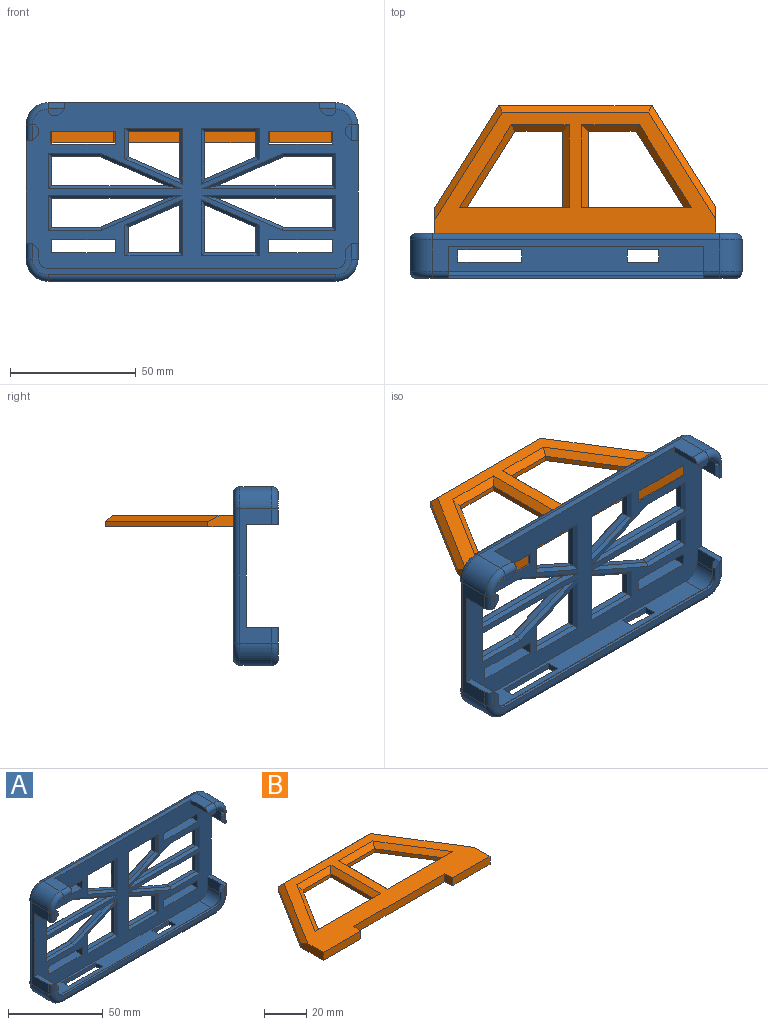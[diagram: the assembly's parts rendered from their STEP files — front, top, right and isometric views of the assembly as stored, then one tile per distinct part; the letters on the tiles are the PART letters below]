
ASSEMBLY  parts=2 mates=1
PART A: 200 faces, bbox 133.5x17.8x72.6 mm
  f0: plane 114.3x10.16mm, normal (0,0,1), area 967.7mm2, adj f8,f9,f12,f91,f192,f193,f194,f195
  f1: plane 114.3x12.7mm, normal (0,0,-1), area 1258.1mm2, adj f17,f18,f96,f106,f192,f193,f194,f195
  f2: plane 6.35x2.54mm, normal (0,-1,0), area 12.1mm2, adj f92,f93,f114,f185,f188
  f3: plane 6.35x2.54mm, normal (0,-1,0), area 12.1mm2, adj f80,f81,f111,f187,f191
  f4: plane 10.16x6.35mm, normal (1,0,0), area 64.5mm2, adj f12,f74,f75,f190
  f5: plane 10.16x6.35mm, normal (-1,0,0), area 64.5mm2, adj f12,f70,f71,f188
  f6: plane 10.16x6.35mm, normal (-1,0,0), area 64.5mm2, adj f8,f12,f77,f91
  f7: plane 10.16x6.35mm, normal (1,0,0), area 64.5mm2, adj f9,f12,f78,f91
  f8: cylinder r=6.35mm len=10.16mm, axis (0,1,0), area 101.3mm2, adj f0,f6,f12,f91
  f9: cylinder r=6.35mm len=10.16mm, axis (0,1,0), area 101.3mm2, adj f0,f7,f12,f91
  f10: plane 10.16x6.35mm, normal (0,0,-1), area 64.5mm2, adj f12,f69,f70,f189
  f11: plane 10.16x6.35mm, normal (0,0,-1), area 64.5mm2, adj f12,f73,f75,f191
  f12: plane 132.08x68.58mm, normal (0,-1,0), area 4649.6mm2, adj f0,f4,f5,f6,f7,f8,f9,f10
  f13: cylinder r=8.89mm len=12.7mm, axis (0,1,0), area 177.3mm2, adj f14,f67,f101,f113
  f14: plane 114.3x12.7mm, normal (0,0,1), area 419.4mm2, adj f12,f13,f15,f69,f73,f103,f111,f112
  f15: cylinder r=8.89mm len=12.7mm, axis (0,1,0), area 177.3mm2, adj f14,f16,f102,f110
  f16: plane 53.34x12.7mm, normal (-1,0,0), area 264.5mm2, adj f12,f15,f17,f74,f78,f100,f108,f109
  f17: cylinder r=8.89mm len=12.7mm, axis (0,1,0), area 177.3mm2, adj f1,f16,f98,f107
  f18: cylinder r=8.89mm len=12.7mm, axis (0,1,0), area 177.3mm2, adj f1,f67,f97,f105
  f19: plane 25.4x5.08mm, normal (0,0,-1), area 129mm2, adj f12,f20,f55,f68
  f20: plane 5.08x5.08mm, normal (-1,0,0), area 25.8mm2, adj f12,f19,f21,f68
  f21: plane 25.4x5.08mm, normal (0,0,1), area 129mm2, adj f12,f20,f55,f68
  f22: plane 25.4x5.08mm, normal (0,0,1), area 129mm2, adj f12,f23,f56,f68
  f23: plane 5.08x5.08mm, normal (1,0,0), area 25.8mm2, adj f12,f22,f24,f68
  f24: plane 25.4x5.08mm, normal (0,0,-1), area 129mm2, adj f12,f23,f56,f68
  f25: plane 5.08x5.08mm, normal (1,0,0), area 25.8mm2, adj f12,f26,f57,f68
  f26: plane 25.4x5.08mm, normal (0,0,-1), area 129mm2, adj f12,f25,f27,f68
  f27: plane 5.08x5.08mm, normal (-1,0,0), area 25.8mm2, adj f12,f26,f57,f68
  f28: plane 5.08x5.08mm, normal (1,0,0), area 25.8mm2, adj f12,f29,f58,f68
  f29: plane 25.4x5.08mm, normal (0,0,-1), area 129mm2, adj f12,f28,f30,f68
  f30: plane 5.08x5.08mm, normal (-1,0,0), area 25.8mm2, adj f12,f29,f58,f68
  f31: plane 26.13x11.43mm, normal (0.4,0,0.92), area 72.4mm2, adj f32,f59,f134,f151
  f32: plane 45.72x2.54mm, normal (0,0,-1), area 116.1mm2, adj f31,f33,f132,f152
  f33: plane 11.43x2.54mm, normal (-1,0,0), area 29mm2, adj f32,f59,f131,f154
  f34: plane 19.05x2.54mm, normal (1,0,0), area 48.4mm2, adj f35,f60,f130,f147
  f35: plane 20.32x8.89mm, normal (-0.4,0,-0.92), area 56.3mm2, adj f34,f36,f129,f148
  f36: plane 10.16x2.54mm, normal (-1,0,0), area 25.8mm2, adj f35,f60,f127,f150
  f37: plane 20.32x2.54mm, normal (0,0,-1), area 51.6mm2, adj f38,f61,f145,f165
  f38: plane 19.05x2.54mm, normal (-1,0,0), area 48.4mm2, adj f37,f39,f143,f163
  f39: plane 20.32x8.89mm, normal (0.4,0,0.92), area 56.3mm2, adj f38,f61,f144,f164
  f40: plane 20.32x8.89mm, normal (0.4,0,-0.92), area 56.3mm2, adj f41,f62,f126,f176
  f41: plane 19.05x2.54mm, normal (-1,0,0), area 48.4mm2, adj f40,f42,f124,f175
  f42: plane 20.32x2.54mm, normal (0,0,1), area 51.6mm2, adj f41,f62,f123,f177
  f43: plane 45.72x2.54mm, normal (0,0,-1), area 116.1mm2, adj f44,f63,f122,f174
  f44: plane 26.13x11.43mm, normal (-0.4,0,0.92), area 72.4mm2, adj f43,f45,f120,f172
  f45: plane 19.59x2.54mm, normal (0,0,1), area 49.8mm2, adj f44,f63,f119,f171
  f46: plane 26.13x11.43mm, normal (-0.4,0,-0.92), area 72.4mm2, adj f47,f64,f118,f170
  f47: plane 45.72x2.54mm, normal (0,0,1), area 116.1mm2, adj f46,f48,f116,f168
  f48: plane 11.43x2.54mm, normal (1,0,0), area 29mm2, adj f47,f64,f115,f167
  f49: plane 19.59x2.54mm, normal (0,0,-1), area 49.8mm2, adj f50,f65,f135,f157
  f50: plane 11.43x2.54mm, normal (-1,0,0), area 29mm2, adj f49,f51,f137,f158
  f51: plane 45.72x2.54mm, normal (0,0,1), area 116.1mm2, adj f50,f65,f138,f156
  f52: plane 19.05x2.54mm, normal (1,0,0), area 48.4mm2, adj f53,f66,f140,f160
  f53: plane 20.32x2.54mm, normal (0,0,-1), area 51.6mm2, adj f52,f54,f139,f162
  f54: plane 10.16x2.54mm, normal (-1,0,0), area 25.8mm2, adj f53,f66,f141,f161
  f55: plane 5.08x5.08mm, normal (1,0,0), area 25.8mm2, adj f12,f19,f21,f68
  f56: plane 5.08x5.08mm, normal (-1,0,0), area 25.8mm2, adj f12,f22,f24,f68
  f57: plane 25.4x5.08mm, normal (0,0,1), area 129mm2, adj f12,f25,f27,f68
  f58: plane 25.4x5.08mm, normal (0,0,1), area 129mm2, adj f12,f28,f30,f68
  f59: plane 19.59x2.54mm, normal (0,0,1), area 49.8mm2, adj f31,f33,f133,f153
  f60: plane 20.32x2.54mm, normal (0,0,1), area 51.6mm2, adj f34,f36,f128,f149
  f61: plane 10.16x2.54mm, normal (1,0,0), area 25.8mm2, adj f37,f39,f146,f166
  f62: plane 10.16x2.54mm, normal (1,0,0), area 25.8mm2, adj f40,f42,f125,f178
  f63: plane 11.43x2.54mm, normal (1,0,0), area 29mm2, adj f43,f45,f121,f173
  f64: plane 19.59x2.54mm, normal (0,0,-1), area 49.8mm2, adj f46,f48,f117,f169
  f65: plane 26.13x11.43mm, normal (0.4,0,-0.92), area 72.4mm2, adj f49,f51,f136,f155
  f66: plane 20.32x8.89mm, normal (-0.4,0,0.92), area 56.3mm2, adj f52,f54,f142,f159
  f67: plane 53.34x12.7mm, normal (1,0,0), area 264.5mm2, adj f12,f13,f18,f71,f77,f99,f104,f114
  f68: plane 127x66.04mm, normal (0,1,0), area 4185.1mm2, adj f19,f20,f21,f22,f23,f24,f25,f26
  f69: plane 12.7x2.54mm, normal (-1,0,0), area 30.9mm2, adj f10,f12,f14,f83,f112
  f70: cylinder r=6.35mm len=12.7mm, axis (0,1,0), area 126.7mm2, adj f5,f10,f12,f82,f93,f113
  f71: plane 12.7x2.54mm, normal (0,0,-1), area 30.9mm2, adj f5,f12,f67,f92,f114
  f72: plane 6.35x2.54mm, normal (0,-1,0), area 12.1mm2, adj f82,f83,f112,f184,f189
  f73: plane 12.7x2.54mm, normal (1,0,0), area 30.9mm2, adj f11,f12,f14,f80,f111
  f74: plane 12.7x2.54mm, normal (0,0,-1), area 30.9mm2, adj f4,f12,f16,f95,f109
  f75: cylinder r=6.35mm len=12.7mm, axis (0,1,0), area 126.7mm2, adj f4,f11,f12,f81,f94,f110
  f76: plane 6.35x2.54mm, normal (0,-1,0), area 12.1mm2, adj f94,f95,f109,f186,f190
  f77: plane 12.7x2.54mm, normal (0,0,1), area 30.9mm2, adj f6,f12,f67,f84,f104
  f78: plane 12.7x2.54mm, normal (0,0,1), area 30.9mm2, adj f7,f12,f16,f90,f108
  f79: plane 127x12.7mm, normal (0,-1,0), area 356.7mm2, adj f84,f85,f86,f87,f88,f89,f90,f104
  f80: plane 2.54x2.54mm, normal (0.71,0,-0.71), area 4.6mm2, adj f3,f73,f191
  f81: plane 2.54x1.27mm, normal (-1,0,0), area 2.4mm2, adj f3,f75,f187,f191
  f82: plane 2.54x1.27mm, normal (1,0,0), area 2.4mm2, adj f70,f72,f184,f189
  f83: plane 2.54x2.54mm, normal (-0.71,0,-0.71), area 4.6mm2, adj f69,f72,f189
  f84: plane 2.54x2.54mm, normal (-0.71,0,0.71), area 8mm2, adj f77,f79,f85,f91,f183
  f85: plane 3.81x1.27mm, normal (-1,0,0), area 4.8mm2, adj f79,f84,f86,f183
  f86: cylinder r=3.81mm len=3.81mm, axis (0,1,0), area 7.6mm2, adj f79,f85,f87,f182
  f87: plane 114.3x1.27mm, normal (0,0,1), area 145.2mm2, adj f79,f86,f88,f181
  f88: cylinder r=3.81mm len=3.81mm, axis (0,1,0), area 7.6mm2, adj f79,f87,f89,f180
  f89: plane 3.81x1.27mm, normal (1,0,0), area 4.8mm2, adj f79,f88,f90,f179
  f90: plane 2.54x2.54mm, normal (0.71,0,0.71), area 8mm2, adj f78,f79,f89,f91,f179
  f91: plane 127x12.7mm, normal (0,1,0), area 182.5mm2, adj f0,f6,f7,f8,f9,f84,f90,f179
  f92: plane 2.54x2.54mm, normal (-0.71,0,-0.71), area 4.6mm2, adj f2,f71,f188
  f93: plane 2.54x1.27mm, normal (0,0,1), area 2.4mm2, adj f2,f70,f185,f188
  f94: plane 2.54x1.27mm, normal (0,0,1), area 2.4mm2, adj f75,f76,f186,f190
  f95: plane 2.54x2.54mm, normal (0.71,0,-0.71), area 4.6mm2, adj f74,f76,f190
  f96: cylinder r=2.54mm len=114.3mm, axis (1,0,0), area 456mm2, adj f1,f68,f97,f98
  f97: torus R=6.35mm, axis (0,-1,0), area 49.9mm2, adj f18,f68,f96,f99
  f98: torus R=6.35mm, axis (0,-1,0), area 49.9mm2, adj f17,f68,f96,f100
  f99: cylinder r=2.54mm len=53.34mm, axis (0,0,1), area 212.8mm2, adj f67,f68,f97,f101
  f100: cylinder r=2.54mm len=53.34mm, axis (0,0,-1), area 212.8mm2, adj f16,f68,f98,f102
  f101: torus R=6.35mm, axis (0,-1,0), area 49.9mm2, adj f13,f68,f99,f103
  f102: torus R=6.35mm, axis (0,-1,0), area 49.9mm2, adj f15,f68,f100,f103
  f103: cylinder r=2.54mm len=114.3mm, axis (-1,0,0), area 456mm2, adj f14,f68,f101,f102
  f104: cylinder r=2.54mm len=6.35mm, axis (0,0,-1), area 25.3mm2, adj f67,f77,f79,f105
  f105: torus R=6.35mm, axis (0,-1,0), area 49.9mm2, adj f18,f79,f104,f106
  f106: cylinder r=2.54mm len=114.3mm, axis (-1,0,0), area 456mm2, adj f1,f79,f105,f107
  f107: torus R=6.35mm, axis (0,-1,0), area 49.9mm2, adj f17,f79,f106,f108
  f108: cylinder r=2.54mm len=6.35mm, axis (0,0,1), area 25.3mm2, adj f16,f78,f79,f107
  f109: cylinder r=2.54mm len=6.35mm, axis (0,0,1), area 25.3mm2, adj f16,f74,f76,f110
  f110: torus R=6.35mm, axis (0,-1,0), area 49.9mm2, adj f15,f75,f109,f111
  f111: cylinder r=2.54mm len=6.35mm, axis (1,0,0), area 25.3mm2, adj f3,f14,f73,f110
  f112: cylinder r=2.54mm len=6.35mm, axis (1,0,0), area 25.3mm2, adj f14,f69,f72,f113
  f113: torus R=6.35mm, axis (0,-1,0), area 49.9mm2, adj f13,f70,f112,f114
  f114: cylinder r=2.54mm len=6.35mm, axis (0,0,-1), area 25.3mm2, adj f2,f67,f71,f113
  f115: plane 13.97x1.27mm, normal (0.71,-0.71,0), area 22.8mm2, adj f12,f48,f116,f117
  f116: plane 53.06x1.27mm, normal (0,-0.71,0.71), area 88.7mm2, adj f12,f47,f115,f118
  f117: plane 21.13x1.27mm, normal (0,-0.71,-0.71), area 36.6mm2, adj f12,f64,f115,f118
  f118: plane 32.2x13.97mm, normal (-0.28,-0.71,-0.65), area 56.9mm2, adj f12,f46,f116,f117
  f119: plane 21.13x1.27mm, normal (0,-0.71,0.71), area 36.6mm2, adj f12,f45,f120,f121
  f120: plane 32.2x13.97mm, normal (-0.28,-0.71,0.65), area 56.9mm2, adj f12,f44,f119,f122
  f121: plane 13.97x1.27mm, normal (0.71,-0.71,0), area 22.8mm2, adj f12,f63,f119,f122
  f122: plane 53.06x1.27mm, normal (0,-0.71,-0.71), area 88.7mm2, adj f12,f43,f120,f121
  f123: plane 22.86x1.27mm, normal (0,-0.71,0.71), area 38.8mm2, adj f12,f42,f124,f125
  f124: plane 22.26x1.27mm, normal (-0.71,-0.71,0), area 37.1mm2, adj f12,f41,f123,f126
  f125: plane 12.26x1.27mm, normal (0.71,-0.71,0), area 20.1mm2, adj f12,f62,f123,f126
  f126: plane 22.86x10.83mm, normal (0.28,-0.71,-0.65), area 42.3mm2, adj f12,f40,f124,f125
  f127: plane 12.26x1.27mm, normal (-0.71,-0.71,0), area 20.1mm2, adj f12,f36,f128,f129
  f128: plane 22.86x1.27mm, normal (0,-0.71,0.71), area 38.8mm2, adj f12,f60,f127,f130
  f129: plane 22.86x10.83mm, normal (-0.28,-0.71,-0.65), area 42.3mm2, adj f12,f35,f127,f130
  f130: plane 22.26x1.27mm, normal (0.71,-0.71,0), area 37.1mm2, adj f12,f34,f128,f129
  f131: plane 13.97x1.27mm, normal (-0.71,-0.71,0), area 22.8mm2, adj f12,f33,f132,f133
  f132: plane 53.06x1.27mm, normal (0,-0.71,-0.71), area 88.7mm2, adj f12,f32,f131,f134
  f133: plane 21.13x1.27mm, normal (0,-0.71,0.71), area 36.6mm2, adj f12,f59,f131,f134
  f134: plane 32.2x13.97mm, normal (0.28,-0.71,0.65), area 56.9mm2, adj f12,f31,f132,f133
  f135: plane 21.13x1.27mm, normal (0,-0.71,-0.71), area 36.6mm2, adj f12,f49,f136,f137
  f136: plane 32.2x13.97mm, normal (0.28,-0.71,-0.65), area 56.9mm2, adj f12,f65,f135,f138
  f137: plane 13.97x1.27mm, normal (-0.71,-0.71,0), area 22.8mm2, adj f12,f50,f135,f138
  f138: plane 53.06x1.27mm, normal (0,-0.71,0.71), area 88.7mm2, adj f12,f51,f136,f137
  f139: plane 22.86x1.27mm, normal (0,-0.71,-0.71), area 38.8mm2, adj f12,f53,f140,f141
  f140: plane 22.26x1.27mm, normal (0.71,-0.71,0), area 37.1mm2, adj f12,f52,f139,f142
  f141: plane 12.26x1.27mm, normal (-0.71,-0.71,0), area 20.1mm2, adj f12,f54,f139,f142
  f142: plane 22.86x10.83mm, normal (-0.28,-0.71,0.65), area 42.3mm2, adj f12,f66,f140,f141
  f143: plane 22.26x1.27mm, normal (-0.71,-0.71,0), area 37.1mm2, adj f12,f38,f144,f145
  f144: plane 22.86x10.83mm, normal (0.28,-0.71,0.65), area 42.3mm2, adj f12,f39,f143,f146
  f145: plane 22.86x1.27mm, normal (0,-0.71,-0.71), area 38.8mm2, adj f12,f37,f143,f146
  f146: plane 12.26x1.27mm, normal (0.71,-0.71,0), area 20.1mm2, adj f12,f61,f144,f145
  f147: plane 22.26x1.27mm, normal (0.71,0.71,0), area 37.1mm2, adj f34,f68,f148,f149
  f148: plane 22.86x10.83mm, normal (-0.28,0.71,-0.65), area 42.3mm2, adj f35,f68,f147,f150
  f149: plane 22.86x1.27mm, normal (0,0.71,0.71), area 38.8mm2, adj f60,f68,f147,f150
  f150: plane 12.26x1.27mm, normal (-0.71,0.71,0), area 20.1mm2, adj f36,f68,f148,f149
  f151: plane 32.2x13.97mm, normal (0.28,0.71,0.65), area 56.9mm2, adj f31,f68,f152,f153
  f152: plane 53.06x1.27mm, normal (0,0.71,-0.71), area 88.7mm2, adj f32,f68,f151,f154
  f153: plane 21.13x1.27mm, normal (0,0.71,0.71), area 36.6mm2, adj f59,f68,f151,f154
  f154: plane 13.97x1.27mm, normal (-0.71,0.71,0), area 22.8mm2, adj f33,f68,f152,f153
  f155: plane 32.2x13.97mm, normal (0.28,0.71,-0.65), area 56.9mm2, adj f65,f68,f156,f157
  f156: plane 53.06x1.27mm, normal (0,0.71,0.71), area 88.7mm2, adj f51,f68,f155,f158
  f157: plane 21.13x1.27mm, normal (0,0.71,-0.71), area 36.6mm2, adj f49,f68,f155,f158
  f158: plane 13.97x1.27mm, normal (-0.71,0.71,0), area 22.8mm2, adj f50,f68,f156,f157
  f159: plane 22.86x10.83mm, normal (-0.28,0.71,0.65), area 42.3mm2, adj f66,f68,f160,f161
  f160: plane 22.26x1.27mm, normal (0.71,0.71,0), area 37.1mm2, adj f52,f68,f159,f162
  f161: plane 12.26x1.27mm, normal (-0.71,0.71,0), area 20.1mm2, adj f54,f68,f159,f162
  f162: plane 22.86x1.27mm, normal (0,0.71,-0.71), area 38.8mm2, adj f53,f68,f160,f161
  f163: plane 22.26x1.27mm, normal (-0.71,0.71,0), area 37.1mm2, adj f38,f68,f164,f165
  f164: plane 22.86x10.83mm, normal (0.28,0.71,0.65), area 42.3mm2, adj f39,f68,f163,f166
  f165: plane 22.86x1.27mm, normal (0,0.71,-0.71), area 38.8mm2, adj f37,f68,f163,f166
  f166: plane 12.26x1.27mm, normal (0.71,0.71,0), area 20.1mm2, adj f61,f68,f164,f165
  f167: plane 13.97x1.27mm, normal (0.71,0.71,0), area 22.8mm2, adj f48,f68,f168,f169
  f168: plane 53.06x1.27mm, normal (0,0.71,0.71), area 88.7mm2, adj f47,f68,f167,f170
  f169: plane 21.13x1.27mm, normal (0,0.71,-0.71), area 36.6mm2, adj f64,f68,f167,f170
  f170: plane 32.2x13.97mm, normal (-0.28,0.71,-0.65), area 56.9mm2, adj f46,f68,f168,f169
  f171: plane 21.13x1.27mm, normal (0,0.71,0.71), area 36.6mm2, adj f45,f68,f172,f173
  f172: plane 32.2x13.97mm, normal (-0.28,0.71,0.65), area 56.9mm2, adj f44,f68,f171,f174
  f173: plane 13.97x1.27mm, normal (0.71,0.71,0), area 22.8mm2, adj f63,f68,f171,f174
  f174: plane 53.06x1.27mm, normal (0,0.71,-0.71), area 88.7mm2, adj f43,f68,f172,f173
  f175: plane 22.26x1.27mm, normal (-0.71,0.71,0), area 37.1mm2, adj f41,f68,f176,f177
  f176: plane 22.86x10.83mm, normal (0.28,0.71,-0.65), area 42.3mm2, adj f40,f68,f175,f178
  f177: plane 22.86x1.27mm, normal (0,0.71,0.71), area 38.8mm2, adj f42,f68,f175,f178
  f178: plane 12.26x1.27mm, normal (0.71,0.71,0), area 20.1mm2, adj f62,f68,f176,f177
  f179: plane 5.08x1.27mm, normal (0.71,0.71,0), area 8mm2, adj f89,f90,f91,f180
  f180: cone r=5.08mm half-angle=45deg, axis (0,1,0), area 12.5mm2, adj f88,f91,f179,f181
  f181: plane 114.3x1.27mm, normal (0,0.71,0.71), area 205.3mm2, adj f87,f91,f180,f182
  f182: cone r=5.08mm half-angle=45deg, axis (0,1,0), area 12.5mm2, adj f86,f91,f181,f183
  f183: plane 5.08x1.27mm, normal (-0.71,0.71,0), area 8mm2, adj f84,f85,f91,f182
  f184: plane 1.27x1.27mm, normal (0.71,0,-0.71), area 1.1mm2, adj f72,f82,f189
  f185: plane 1.27x1.27mm, normal (-0.71,0,0.71), area 1.1mm2, adj f2,f93,f188
  f186: plane 1.27x1.27mm, normal (0.71,0,0.71), area 1.1mm2, adj f76,f94,f190
  f187: plane 1.27x1.27mm, normal (-0.71,0,-0.71), area 1.1mm2, adj f3,f81,f191
  f188: plane 6.35x2.54mm, normal (-0.71,0.71,0), area 17.1mm2, adj f2,f5,f92,f93,f185
  f189: plane 6.35x2.54mm, normal (0,0.71,-0.71), area 17.1mm2, adj f10,f72,f82,f83,f184
  f190: plane 6.35x2.54mm, normal (0.71,0.71,0), area 17.1mm2, adj f4,f76,f94,f95,f186
  f191: plane 6.35x2.54mm, normal (0,0.71,-0.71), area 17.1mm2, adj f3,f11,f80,f81,f187
  f192: plane 5.08x2.54mm, normal (-1,0,0), area 12.9mm2, adj f0,f1,f193,f195
  f193: plane 12.7x2.54mm, normal (0,1,0), area 32.3mm2, adj f0,f1,f192,f194
  f194: plane 5.08x2.54mm, normal (1,0,0), area 12.9mm2, adj f0,f1,f193,f195
  f195: plane 12.7x2.54mm, normal (0,-1,0), area 32.3mm2, adj f0,f1,f192,f194
  f196: plane 5.08x2.54mm, normal (-1,0,0), area 12.9mm2, adj f0,f1,f197,f199
  f197: plane 25.4x2.54mm, normal (0,1,0), area 64.5mm2, adj f0,f1,f196,f198
  f198: plane 5.08x2.54mm, normal (1,0,0), area 12.9mm2, adj f0,f1,f197,f199
  f199: plane 25.4x2.54mm, normal (0,-1,0), area 64.5mm2, adj f0,f1,f196,f198
PART B: 29 faces, bbox 111.8x55.9x4.6 mm
  f0: plane 30.48x19.05mm, normal (-0.85,-0.53,0), area 73mm2, adj f1,f17,f19,f23
  f1: plane 43.64x4.57mm, normal (0,1,0), area 181.2mm2, adj f0,f2,f18,f19,f23,f25
  f2: plane 30.48x2.03mm, normal (1,0,0), area 61.9mm2, adj f1,f17,f19,f25
  f3: plane 5.08x4.57mm, normal (-1,-0.09,0), area 23.3mm2, adj f4,f15,f18,f19
  f4: plane 24.96x4.57mm, normal (0,-1,0), area 114.1mm2, adj f3,f5,f18,f19
  f5: plane 15.24x4.57mm, normal (1,0,0), area 63.6mm2, adj f4,f6,f18,f19,f28
  f6: plane 40.64x25.4mm, normal (0.85,0.53,0), area 97.4mm2, adj f5,f7,f19,f28
  f7: plane 60.96x2.03mm, normal (0,1,0), area 123.9mm2, adj f6,f8,f19,f27
  f8: plane 40.64x25.4mm, normal (-0.85,0.53,0), area 97.4mm2, adj f7,f9,f19,f26
  f9: plane 15.24x4.57mm, normal (-1,0,0), area 63.6mm2, adj f8,f10,f18,f19,f26
  f10: plane 24.96x4.57mm, normal (0,-1,0), area 114.1mm2, adj f9,f11,f18,f19
  f11: plane 5.08x4.57mm, normal (1,-0.09,0), area 23.3mm2, adj f10,f15,f18,f19
  f12: plane 30.48x19.05mm, normal (0.85,-0.53,0), area 73mm2, adj f13,f16,f19,f22
  f13: plane 19.05x2.03mm, normal (0,-1,0), area 38.7mm2, adj f12,f14,f19,f21
  f14: plane 30.48x2.03mm, normal (-1,0,0), area 61.9mm2, adj f13,f16,f19,f20
  f15: plane 60.96x4.57mm, normal (0,-1,0), area 278.7mm2, adj f3,f11,f18,f19
  f16: plane 43.64x4.57mm, normal (0,1,0), area 181.2mm2, adj f12,f14,f18,f19,f20,f22
  f17: plane 19.05x2.03mm, normal (0,-1,0), area 38.7mm2, adj f0,f2,f19,f24
  f18: plane 111.76x53.34mm, normal (0,0,1), area 2299.3mm2, adj f1,f3,f4,f5,f9,f10,f11,f15
  f19: plane 111.76x55.88mm, normal (0,0,-1), area 3159mm2, adj f0,f1,f2,f3,f4,f5,f6,f7
  f20: plane 33.02x2.54mm, normal (-0.71,0,0.71), area 114mm2, adj f14,f16,f18,f21
  f21: plane 23x2.54mm, normal (0,-0.71,0.71), area 75.5mm2, adj f13,f18,f20,f22
  f22: plane 33.02x22.05mm, normal (0.6,-0.37,0.71), area 134.5mm2, adj f12,f16,f18,f21
  f23: plane 33.02x22.05mm, normal (-0.6,-0.37,0.71), area 134.5mm2, adj f0,f1,f18,f24
  f24: plane 23x2.54mm, normal (0,-0.71,0.71), area 75.5mm2, adj f17,f18,f23,f25
  f25: plane 33.02x2.54mm, normal (0.71,0,0.71), area 114mm2, adj f1,f2,f18,f24
  f26: plane 45.43x26.81mm, normal (-0.6,0.37,0.71), area 176.9mm2, adj f8,f9,f18,f27
  f27: plane 60.96x2.54mm, normal (0,0.71,0.71), area 213.9mm2, adj f7,f18,f26,f28
  f28: plane 45.43x26.81mm, normal (0.6,0.37,0.71), area 176.9mm2, adj f5,f6,f18,f27
PLACE A t=(1.35,4.59,-3.81)mm
PLACE B t=(1.13,-0.49,15.75)mm
MATE fastened B.f4 <-> A.f12  axis (0,-1,0) through (44.53,-0.49,20.32)mm
